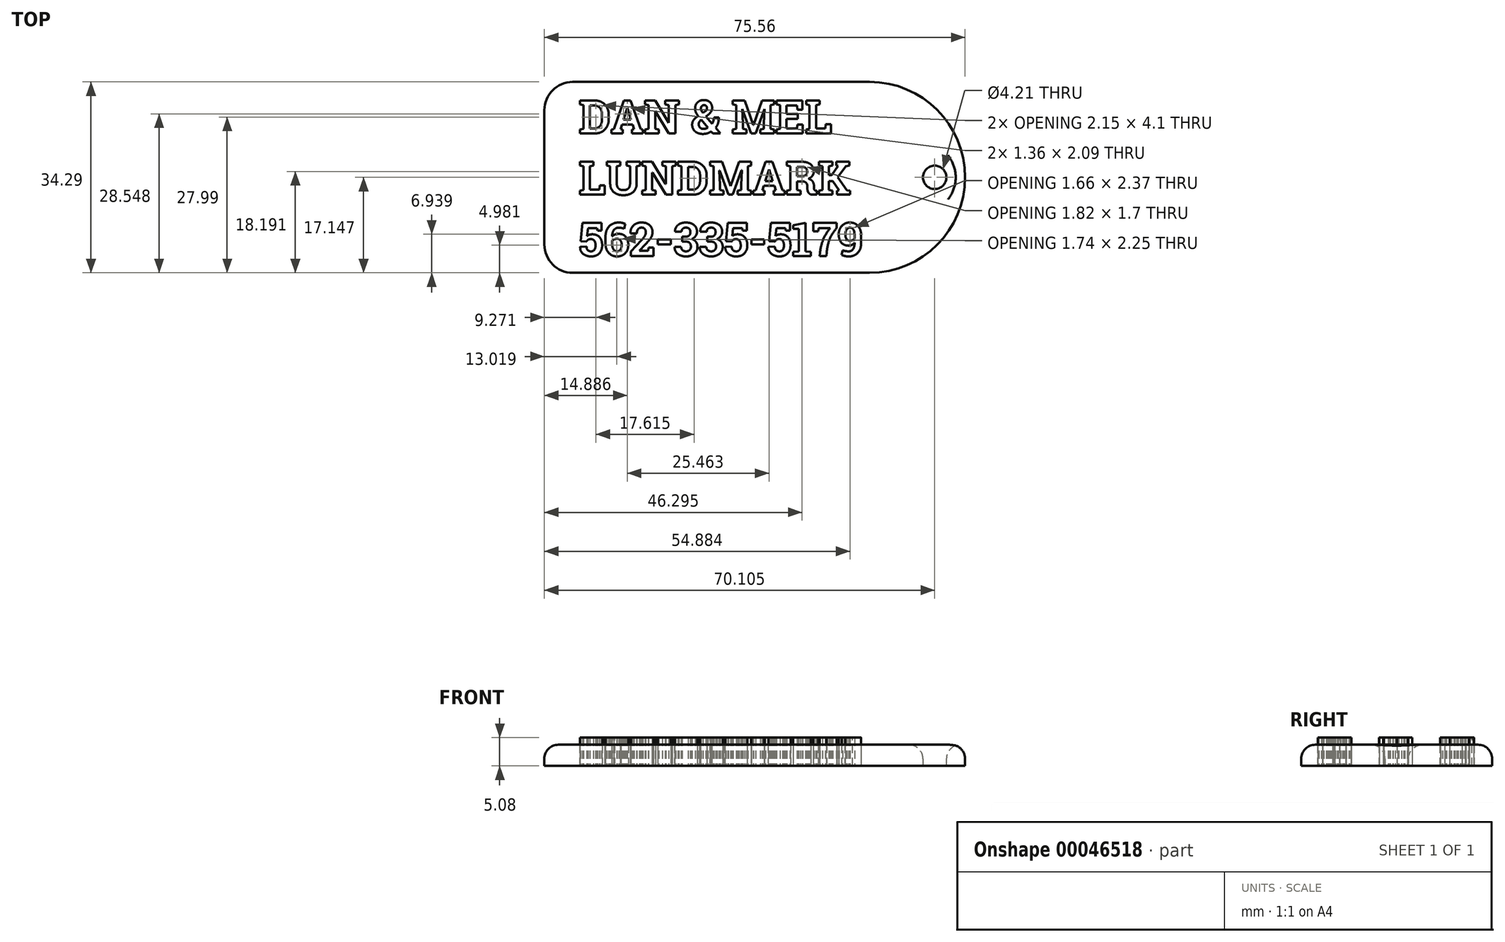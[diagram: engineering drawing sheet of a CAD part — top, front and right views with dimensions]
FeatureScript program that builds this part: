
annotation { "Feature Type Name" : "Feature", "Feature Type Description" : "" }
export const myFeature = defineFeature(function(context is Context, id is Id, definition is map)
    precondition{}
    {
        {
            var Q0;
            Q0=qCreatedBy(makeId("Top.planeOp"),FACE);
            var sketch = newSketch(context, id + "F0", { "sketchPlane" : qUnion([Q0])});
            skText(sketch, "E0", { "text": "DAN & MEL\nLUNDMARK\n562-335-5179", "fontName": "RobotoSlab-Bold.ttf"});
            const initialGuessF0  = {"E0": [-0.0031, -0.00307, 1, 0, 0.006]};
            skSetInitialGuess(sketch, initialGuessF0);
            skSolve(sketch);
        }
        {
            var Q0;
            Q0 = qSketchRegion(id + "F0", true);
            extrude(context, id + "F1", {"entities" : qUnion([Q0]), "depth" : 5.08 * mm});
        }
        {
            var Q0;
            Q0=qCreatedBy(makeId("Top.planeOp"),FACE);
            var sketch = newSketch(context, id + "F2", { "sketchPlane" : qUnion([Q0])});
            skLineSegment(sketch, "E1.bottom", {"start": v(-9.25, 6.2) * mm, "end": v(49.17, 6.2) * mm});
            skLineSegment(sketch, "E1.top", {"start": v(-9.25, -28.1) * mm, "end": v(49.17, -28.1) * mm});
            skLineSegment(sketch, "E1.left", {"start": v(-9.25, 6.2) * mm, "end": v(-9.25, -28.1) * mm});
            skLineSegment(sketch, "E1.right", {"start": v(49.17, 6.2) * mm, "end": v(49.17, -28.1) * mm});
            skArc(sketch, "E2", {"start": v(49.17, -28.1) * mm, "mid": v(66.31, -10.95) * mm, "end": v(49.17, 6.2) * mm});
            skCircle(sketch, "E3", {"center": v(60.85, -10.95) * mm, "radius": 2.1 * mm});
            skSolve(sketch);
        }
        {
            var Q0;
            Q0=makeQuery(id+"F2.imprint","IMPRINT",FACE,{"disambiguationData":[TD([[makeQuery(id+"F2.imprint","IMPRINT",EDGE,{"derivedFrom":sQuery(id+"F2.wireOp",EDGE,"E1.bottom")}),-1.0]])]});
            var Q1;
            Q1=makeQuery(id+"F2.imprint","IMPRINT",FACE,{"disambiguationData":[TD([[makeQuery(id+"F2.imprint","IMPRINT",EDGE,{"derivedFrom":sQuery(id+"F2.wireOp",EDGE,"E1.right")}),1.0]])]});
            extrude(context, id + "F3", {"entities" : qUnion([Q0, Q1]), "depth" : 3.8 * mm});
        }
        {
            var Q0;
            Q0=makeQuery(id+"F3.opExtrude","SWEPT_EDGE",EDGE,{"disambiguationData":[OSD([sQuery(id+"F2.wireOp",EDGE,"E1.bottom"),sQuery(id+"F2.wireOp",EDGE,"E1.left")])]});
            var Q1;
            Q1=makeQuery(id+"F3.opExtrude","SWEPT_EDGE",EDGE,{"disambiguationData":[OSD([sQuery(id+"F2.wireOp",EDGE,"E1.top"),sQuery(id+"F2.wireOp",EDGE,"E1.left")])]});
            fillet(context, id + "F4", {"entities" : qUnion([Q0, Q1]), "radius" : 5.08 * mm, "tangentPropagation" : true, "allowEdgeOverflow" : false});
        }
        {
            var Q0;
            Q0=makeQuery(id+"F3.opExtrude","CAP_FACE",FACE,{"disambiguationData":[OSD([sQuery(id+"F2.wireOp",EDGE,"E1.bottom"),sQuery(id+"F2.wireOp",EDGE,"E1.top"),sQuery(id+"F2.wireOp",EDGE,"E1.left"),sQuery(id+"F2.wireOp",EDGE,"E2"),sQuery(id+"F2.wireOp",EDGE,"E3")])],"isStart":false});
            fillet(context, id + "F5", {"entities" : qUnion([Q0]), "radius" : 2.54 * mm, "tangentPropagation" : true, "allowEdgeOverflow" : false});
        }
    });
